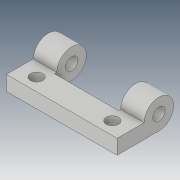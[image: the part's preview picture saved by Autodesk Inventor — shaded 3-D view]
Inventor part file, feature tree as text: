
AUTODESK INVENTOR PART (.ipt)
format: ipt  version: 2019 (Build 230136000, 136)  size: 178,688 bytes
history: native  units: mm
features: extrude x6, sketch x5, plane x5, other x3, move_body x2, fillet x1, direct_edit x1, projected_geometry x1
ambient origin geometry x8: Origin, YZ Plane, XZ Plane, XY Plane, X Axis, Y Axis, Z Axis, Center Point
bodies: Solid1 (feature_tree)
feature tree (24):
  extrude  "Extrusion1"  Depth=45.0mm
  sketch  "Sketch4"  dims[d5=5.0mm d6=5.0mm d7=11.0mm]
  extrude  "Extrusion4"  Depth=5.0mm
  fillet  "Fillet1"  Radius=11.0mm
  extrude  "Extrusion5"  Depth=23.0mm
  plane  "Work Plane1"
  extrude  "Extrusion6"  Depth=12.0mm
  plane  "Work Plane8"
  plane  "Work Plane10"
  sketch  "Sketch11"  dims[d21=0.0mm d24=3.0mm d25=0.0mm d26=12.0mm d27=5.0mm d28=3.0mm d29=0.0mm d33=5.0mm d34=5.0mm d35=17.8mm d36=7.0mm d37=17.8mm d38=7.1mm d39=30.8mm d40=7.1mm d41=3.0mm d42=0.0mm d52=0.0mm d53=0.0mm d54=0.0mm d55=10.0mm d56=0.0mm d57=10.0mm d58=0.0mm d59=0.0mm d60=0.0mm d61=-1.5mm d62=0.0mm d63=0.0mm d64=-1.5mm]
  plane  "Work Plane11"
  plane  "Work Plane12"
  extrude  "Extrusion10"  Depth=10.0mm TaperAngle=0.0deg
  extrude  "Extrusion11"  Depth=12.0mm
  direct_edit  "Direct Edit1"
  sketch  "Sketch1"  dims[d0=6.0mm d1=0.0mm d4=45.0mm]
  sketch  "Sketch5"  dims[d8=11.0mm d9=23.0mm]
  sketch  "Sketch6"  dims[d10=10.0mm d20=12.0mm]
  projected_geometry  "Projected Loop4"
  move_body  "Move1"
  move_body  "Move2"
  parser-record x1  (decoder bookkeeping rows leaked as tree rows — omitted from the tree; the rows remain in map.json)
  other  "Cerniera Assemb.iam"
  other  "Cerniera 1:2"
note: 1 file-system path scrubbed to <path> (originals preserved in map.json)
